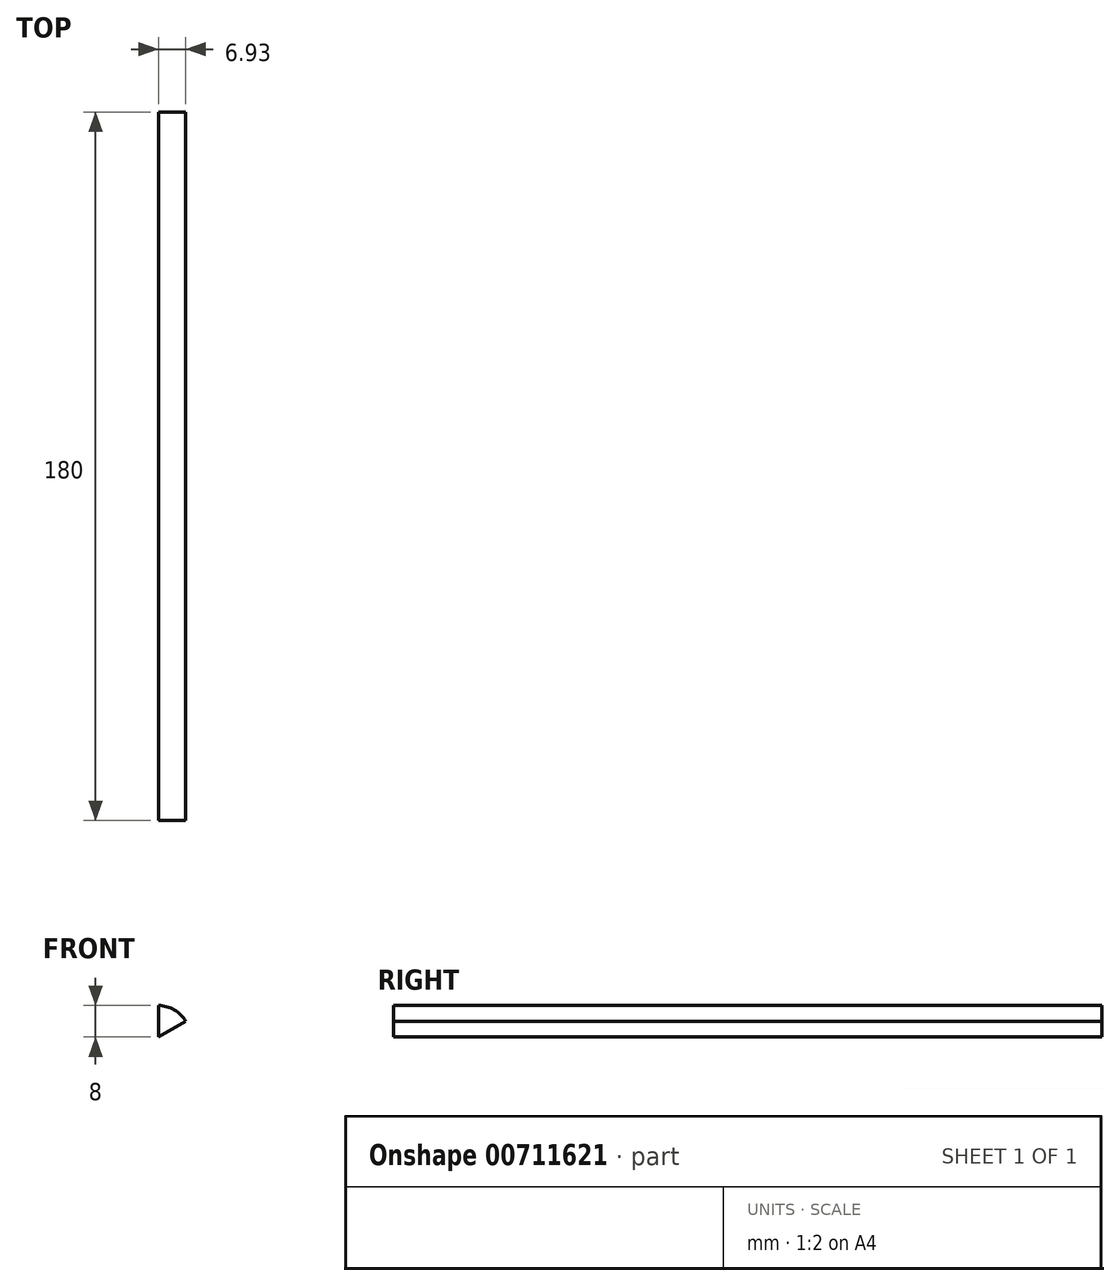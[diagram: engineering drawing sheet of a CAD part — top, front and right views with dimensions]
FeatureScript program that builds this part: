
annotation { "Feature Type Name" : "Feature", "Feature Type Description" : "" }
export const myFeature = defineFeature(function(context is Context, id is Id, definition is map)
    precondition{}
    {
        {
            var Q0;
            Q0=qCreatedBy(makeId("Right.planeOp"),FACE);
            var sketch = newSketch(context, id + "F0", { "sketchPlane" : qUnion([Q0])});
            skLineSegment(sketch, "E0.bottom", {"start": v(-90.04, 7.69) * mm, "end": v(89.96, 7.69) * mm});
            skLineSegment(sketch, "E0.top", {"start": v(-90.04, -0.31) * mm, "end": v(89.96, -0.31) * mm});
            skLineSegment(sketch, "E0.left", {"start": v(-90.04, 7.69) * mm, "end": v(-90.04, -0.31) * mm});
            skLineSegment(sketch, "E0.right", {"start": v(89.96, 7.69) * mm, "end": v(89.96, -0.31) * mm});
            skSolve(sketch);
        }
        {
            var Q0;
            Q0 = qSketchRegion(id + "F0", true);
            var Q1;
            Q1=sQuery(id+"F0.wireOp",EDGE,"E0.top");
            revolve(context, id + "F1", {"surfaceOperationType" : NewSurfaceOperationType.NEW, "entities" : qUnion([Q0]), "axis" : qUnion([Q1]), "revolveType" : RevolveType.ONE_DIRECTION, "angle" : 60 * degree});
        }
    });
